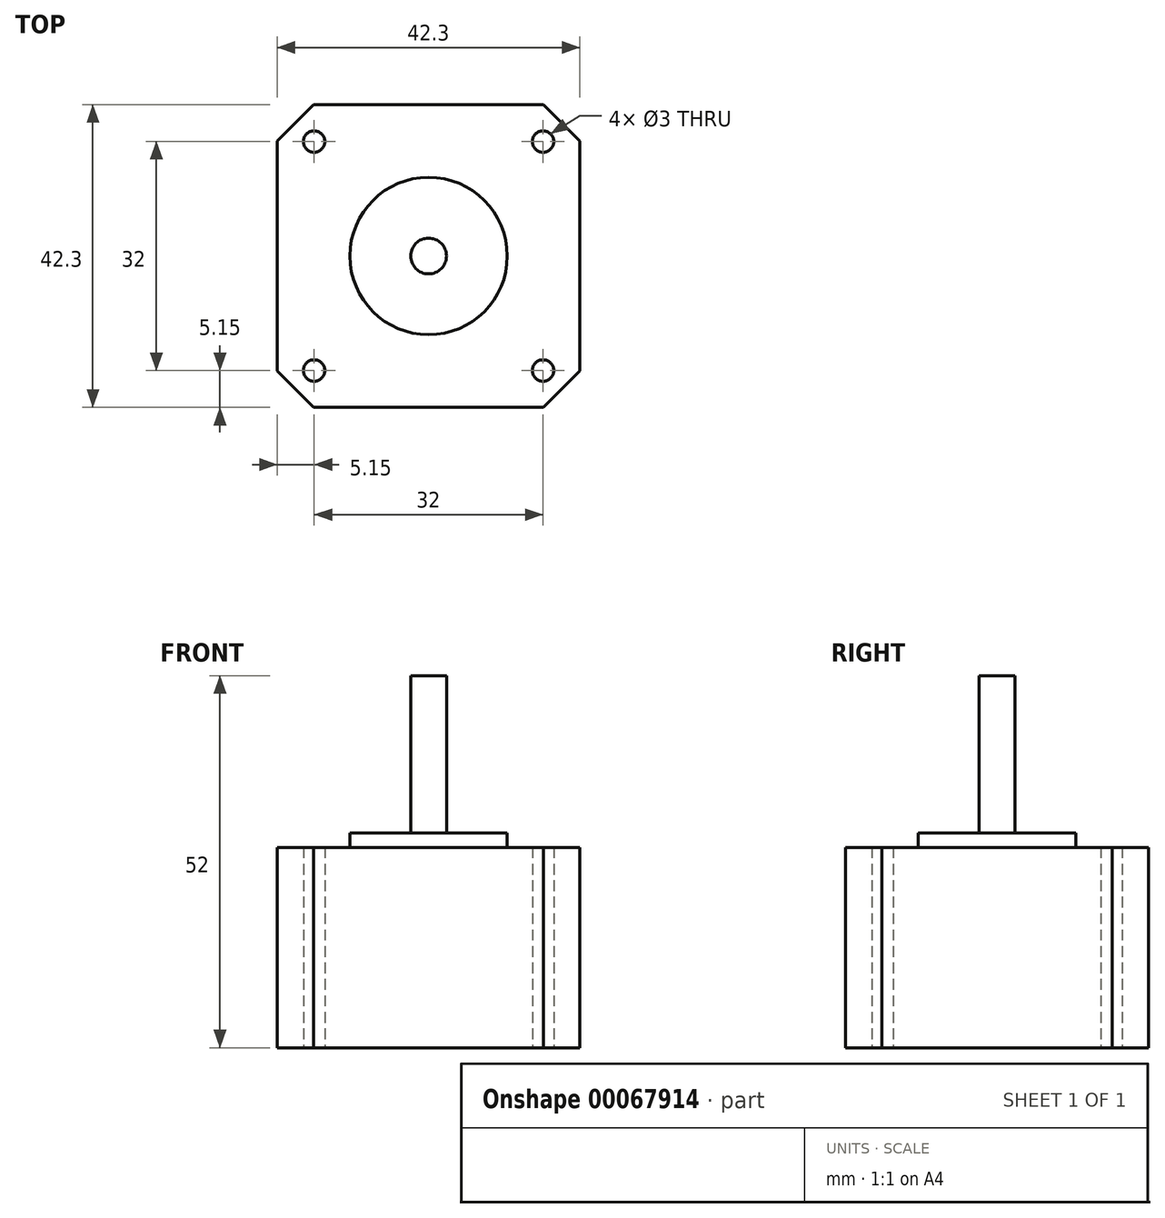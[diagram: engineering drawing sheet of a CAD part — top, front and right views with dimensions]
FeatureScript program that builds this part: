
annotation { "Feature Type Name" : "Feature", "Feature Type Description" : "" }
export const myFeature = defineFeature(function(context is Context, id is Id, definition is map)
    precondition{}
    {
        {
            var Q0;
            Q0=qCreatedBy(makeId("Top.planeOp"),FACE);
            var sketch = newSketch(context, id + "F0", { "sketchPlane" : qUnion([Q0])});
            skLineSegment(sketch, "E0.bottom", {"start": v(21.15, 21.15) * mm, "end": v(-21.15, 21.15) * mm});
            skLineSegment(sketch, "E0.top", {"start": v(21.15, -21.15) * mm, "end": v(-21.15, -21.15) * mm});
            skLineSegment(sketch, "E0.left", {"start": v(21.15, 21.15) * mm, "end": v(21.15, -21.15) * mm});
            skLineSegment(sketch, "E0.right", {"start": v(-21.15, 21.15) * mm, "end": v(-21.15, -21.15) * mm});
            skPoint(sketch, "E0.middle", {"position": v(0, 0) * mm});
            skSolve(sketch);
        }
        {
            var Q0;
            Q0=makeQuery(id+"F0.imprint","IMPRINT",FACE,{"disambiguationData":[TD([[makeQuery(id+"F0.imprint","IMPRINT",EDGE,{"derivedFrom":sQuery(id+"F0.wireOp",EDGE,"E0.bottom")}),1.0]])]});
            extrude(context, id + "F1", {"entities" : qUnion([Q0]), "depth" : 28 * mm});
        }
        {
            var Q0;
            Q0=makeQuery(id+"F1.opExtrude","CAP_FACE",FACE,{"disambiguationData":[OSD([sQuery(id+"F0.wireOp",EDGE,"E0.bottom"),sQuery(id+"F0.wireOp",EDGE,"E0.top"),sQuery(id+"F0.wireOp",EDGE,"E0.left"),sQuery(id+"F0.wireOp",EDGE,"E0.right")])],"isStart":false});
            var sketch = newSketch(context, id + "F2", { "sketchPlane" : qUnion([Q0])});
            skCircle(sketch, "E1", {"center": v(0, 0) * mm, "radius": 11 * mm});
            skSolve(sketch);
        }
        {
            var Q0;
            Q0=makeQuery(id+"F2.imprint","IMPRINT",FACE,{"disambiguationData":[TD([[makeQuery(id+"F2.imprint","IMPRINT",EDGE,{"derivedFrom":sQuery(id+"F2.wireOp",EDGE,"E1")}),1.0]])]});
            extrude(context, id + "F3", {"entities" : qUnion([Q0]), "operationType" : NewBodyOperationType.ADD, "depth" : 2 * mm});
        }
        {
            var Q0;
            Q0=makeQuery(id+"F1.opExtrude","CAP_FACE",FACE,{"disambiguationData":[OSD([sQuery(id+"F0.wireOp",EDGE,"E0.bottom"),sQuery(id+"F0.wireOp",EDGE,"E0.top"),sQuery(id+"F0.wireOp",EDGE,"E0.left"),sQuery(id+"F0.wireOp",EDGE,"E0.right")])],"isStart":false});
            var sketch = newSketch(context, id + "F4", { "sketchPlane" : qUnion([Q0])});
            skCircle(sketch, "E2", {"center": v(0, 0) * mm, "radius": 2.5 * mm});
            skSolve(sketch);
        }
        {
            var Q0;
            Q0 = qSketchRegion(id + "F4", true);
            extrude(context, id + "F5", {"entities" : qUnion([Q0]), "operationType" : NewBodyOperationType.ADD, "depth" : 24 * mm});
        }
        {
            var Q0;
            Q0=qCreatedBy(makeId("Top.planeOp"),FACE);
            var sketch = newSketch(context, id + "F6", { "sketchPlane" : qUnion([Q0])});
            skLineSegment(sketch, "E3.bottom", {"start": v(16, 16) * mm, "end": v(-16, 16) * mm});
            skLineSegment(sketch, "E3.top", {"start": v(16, -16) * mm, "end": v(-16, -16) * mm});
            skLineSegment(sketch, "E3.left", {"start": v(16, 16) * mm, "end": v(16, -16) * mm});
            skLineSegment(sketch, "E3.right", {"start": v(-16, 16) * mm, "end": v(-16, -16) * mm});
            skPoint(sketch, "E3.middle", {"position": v(0, 0) * mm});
            skSolve(sketch);
        }
        {
            var Q0;
            Q0=sQuery(id+"F6.wireOp",VERTEX,"E3.right.start");
            var Q1;
            Q1=sQuery(id+"F6.wireOp",VERTEX,"E3.left.start");
            var Q2;
            Q2=sQuery(id+"F6.wireOp",VERTEX,"E3.right.end");
            var Q3;
            Q3=sQuery(id+"F6.wireOp",VERTEX,"E3.top.start");
            var Q4;
            Q4=makeQuery(id+"F1.opExtrude","SWEPT_BODY",BODY,{"disambiguationData":[OSD([sQuery(id+"F0.wireOp",EDGE,"E0.bottom"),sQuery(id+"F0.wireOp",EDGE,"E0.top"),sQuery(id+"F0.wireOp",EDGE,"E0.left"),sQuery(id+"F0.wireOp",EDGE,"E0.right")])]});
            hole(context, id + "F7", {"style" : HoleStyle.SIMPLE, "endStyle" : HoleEndStyle.THROUGH, "oppositeDirection" : true, "holeDiameter" : 3 * mm, "locations" : qUnion([Q0, Q1, Q2, Q3]), "scope" : qUnion([Q4]), "isTappedThrough" : true});
        }
        {
            var Q0;
            Q0=makeQuery(id+"F1.opExtrude","SWEPT_EDGE",EDGE,{"disambiguationData":[OSD([sQuery(id+"F0.wireOp",EDGE,"E0.top"),sQuery(id+"F0.wireOp",EDGE,"E0.right")])]});
            var Q1;
            Q1=makeQuery(id+"F1.opExtrude","SWEPT_EDGE",EDGE,{"disambiguationData":[OSD([sQuery(id+"F0.wireOp",EDGE,"E0.top"),sQuery(id+"F0.wireOp",EDGE,"E0.left")])]});
            var Q2;
            Q2=makeQuery(id+"F1.opExtrude","SWEPT_EDGE",EDGE,{"disambiguationData":[OSD([sQuery(id+"F0.wireOp",EDGE,"E0.bottom"),sQuery(id+"F0.wireOp",EDGE,"E0.left")])]});
            var Q3;
            Q3=makeQuery(id+"F1.opExtrude","SWEPT_EDGE",EDGE,{"disambiguationData":[OSD([sQuery(id+"F0.wireOp",EDGE,"E0.bottom"),sQuery(id+"F0.wireOp",EDGE,"E0.right")])]});
            chamfer(context, id + "F8", {"entities" : qUnion([Q0, Q1, Q2, Q3]), "width" : 5.08 * mm, "tangentPropagation" : true});
        }
    });
